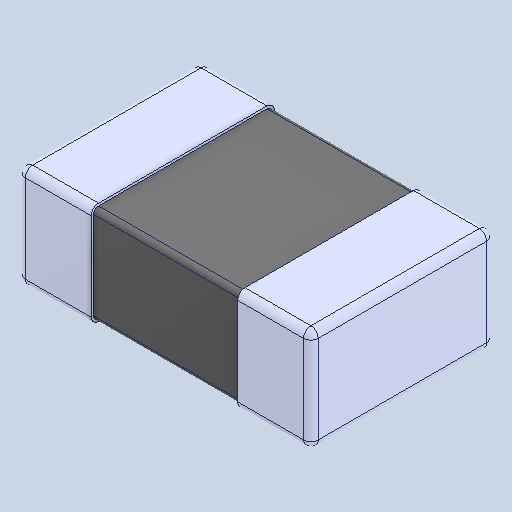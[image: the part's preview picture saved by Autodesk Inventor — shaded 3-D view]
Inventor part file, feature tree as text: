
AUTODESK INVENTOR PART (.ipt)
format: ipt  version: 2025 (Build 290162000, 162)  size: 131,072 bytes
history: native  units: mm
features: fillet x1, other x1, mirror x1
ambient origin geometry x8: Origin, YZ Plane, XZ Plane, XY Plane, X Axis, Y Axis, Z Axis, Center Point
bodies: Solid1 (feature_tree), Solid2 (feature_tree), Solid3 (feature_tree)
feature tree (3):
  fillet  "Fillet1"  [1 undecoded]
  other  "Boss-Extrude2"
  mirror  "Mirror2"
note: 1 required parameter value undecoded (feature->parameter linkage not recoverable at this tier; creation-order binding heuristic only, values carry confidence <= 0.55)
